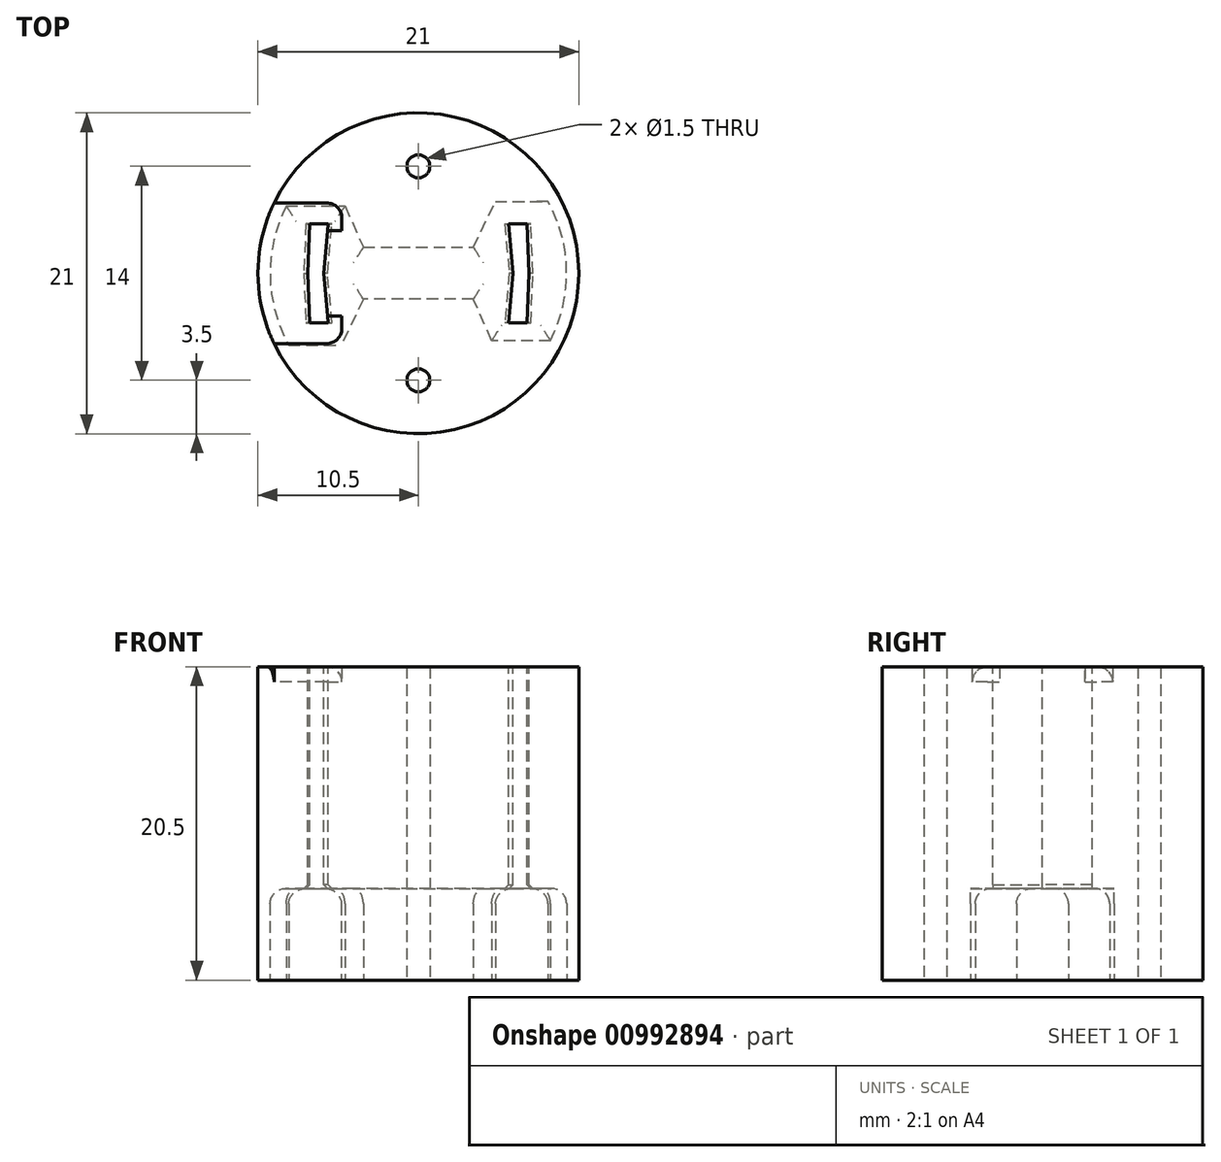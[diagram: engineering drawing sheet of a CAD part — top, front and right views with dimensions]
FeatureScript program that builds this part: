
annotation { "Feature Type Name" : "Feature", "Feature Type Description" : "" }
export const myFeature = defineFeature(function(context is Context, id is Id, definition is map)
    precondition{}
    {
        {
            var Q0;
            Q0=qCreatedBy(makeId("Top.planeOp"),FACE);
            var sketch = newSketch(context, id + "F0", { "sketchPlane" : qUnion([Q0])});
            skCircle(sketch, "E0", {"center": v(0, 0) * mm, "radius": 10.5 * mm});
            skSolve(sketch);
        }
        {
            var Q0;
            Q0=qSketchRegion(id+"F0",true);
            extrude(context, id + "F1", {"entities" : qUnion([Q0]), "oppositeDirection" : true, "depth" : 20.5 * mm});
        }
        {
            var Q0;
            Q0=makeQuery(id+"F1.opExtrude","CAP_FACE",FACE,{"disambiguationData":[OSD([sQuery(id+"F0.wireOp",EDGE,"E0")])],"isStart":false});
            var sketch = newSketch(context, id + "F2", { "sketchPlane" : qUnion([Q0])});
            skArc(sketch, "E1", {"start": v(-6.4, -5.2) * mm, "mid": v(-0.2, -8.25) * mm, "end": v(6.15, -5.5) * mm});
            skLineSegment(sketch, "E2", {"start": v(-8.49, 4.7) * mm, "end": v(-5.04, 4.7) * mm});
            skLineSegment(sketch, "E3", {"start": v(-8.64, -4.4) * mm, "end": v(-4.8, -4.4) * mm});
            skLineSegment(sketch, "E4", {"start": v(8.64, 4.4) * mm, "end": v(4.8, 4.4) * mm});
            skLineSegment(sketch, "E5", {"start": v(4.8, 4.4) * mm, "end": v(3.6, 1.7) * mm});
            skLineSegment(sketch, "E6", {"start": v(3.6, 1.7) * mm, "end": v(-3.6, 1.7) * mm});
            skLineSegment(sketch, "E7", {"start": v(-3.6, 1.7) * mm, "end": v(-5.04, 4.7) * mm});
            skLineSegment(sketch, "E8", {"start": v(-4, 4.4) * mm, "end": v(3.92, 4.4) * mm});
            skLineSegment(sketch, "E9", {"start": v(3.92, 4.4) * mm, "end": v(3.17, 2.7) * mm});
            skLineSegment(sketch, "E10", {"start": v(3.17, 2.7) * mm, "end": v(-3.2, 2.7) * mm});
            skLineSegment(sketch, "E11", {"start": v(-3.2, 2.7) * mm, "end": v(-4, 4.4) * mm});
            skLineSegment(sketch, "E12", {"start": v(-4.8, -4.4) * mm, "end": v(-3.6, -1.7) * mm});
            skLineSegment(sketch, "E13", {"start": v(-3.6, -1.7) * mm, "end": v(3.6, -1.7) * mm});
            skLineSegment(sketch, "E14", {"start": v(4, -4.4) * mm, "end": v(3.2, -2.7) * mm});
            skLineSegment(sketch, "E15", {"start": v(3.2, -2.7) * mm, "end": v(-3.17, -2.7) * mm});
            skLineSegment(sketch, "E16", {"start": v(-3.17, -2.7) * mm, "end": v(-3.92, -4.4) * mm});
            skLineSegment(sketch, "E17", {"start": v(-3.92, -4.4) * mm, "end": v(4, -4.4) * mm});
            skArc(sketch, "E18", {"start": v(-8.64, -4.4) * mm, "mid": v(-9.7, 0.17) * mm, "end": v(-8.49, 4.7) * mm});
            skArc(sketch, "E19", {"start": v(8.64, 4.4) * mm, "mid": v(9.7, -0.17) * mm, "end": v(8.49, -4.7) * mm});
            skLineSegment(sketch, "E20", {"start": v(6.15, -5.5) * mm, "end": v(2.15, -5.5) * mm});
            skLineSegment(sketch, "E21", {"start": v(3.6, -1.7) * mm, "end": v(5.04, -4.7) * mm});
            skLineSegment(sketch, "E22", {"start": v(5.04, -4.7) * mm, "end": v(8.49, -4.7) * mm});
            skLineSegment(sketch, "E23", {"start": v(-2.15, 5.5) * mm, "end": v(-6.15, 5.5) * mm});
            skLineSegment(sketch, "E24.trimOffspring", {"start": v(6.4, 5.2) * mm, "end": v(-2.15, 5.2) * mm});
            skArc(sketch, "E25.trimOffspring", {"start": v(-6.15, 5.5) * mm, "mid": v(0.2, 8.25) * mm, "end": v(6.4, 5.2) * mm});
            skLineSegment(sketch, "E26.trimOffspring", {"start": v(2.15, -5.2) * mm, "end": v(-6.4, -5.2) * mm});
            skLineSegment(sketch, "E27", {"start": v(2.15, -5.2) * mm, "end": v(2.15, -5.5) * mm});
            skLineSegment(sketch, "E28", {"start": v(-2.15, 5.5) * mm, "end": v(-2.15, 5.2) * mm});
            skSolve(sketch);
        }
        {
            var Q0;
            Q0=qSketchRegion(id+"F2",true);
            extrude(context, id + "F3", {"entities" : qUnion([Q0]), "operationType" : NewBodyOperationType.REMOVE, "oppositeDirection" : true, "depth" : 6 * mm});
        }
        {
            var Q0;
            Q0=makeQuery(id+"F1.opExtrude","CAP_FACE",FACE,{"disambiguationData":[OSD([sQuery(id+"F0.wireOp",EDGE,"E0")])],"isStart":false});
            var sketch = newSketch(context, id + "F4", { "sketchPlane" : qUnion([Q0])});
            skCircle(sketch, "E29", {"center": v(0, -7) * mm, "radius": 0.75 * mm});
            skCircle(sketch, "E30", {"center": v(0, 7) * mm, "radius": 0.75 * mm});
            skSolve(sketch);
        }
        {
            var Q0;
            Q0=qSketchRegion(id+"F4",true);
            extrude(context, id + "F5", {"entities" : qUnion([Q0]), "operationType" : NewBodyOperationType.REMOVE, "endBound" : BoundingType.THROUGH_ALL, "oppositeDirection" : true, "depth" : 30 * mm});
        }
        {
            var Q0;
            Q0=makeQuery(id+"F1.opExtrude","CAP_FACE",FACE,{"disambiguationData":[OSD([sQuery(id+"F0.wireOp",EDGE,"E0")])],"isStart":true});
            var sketch = newSketch(context, id + "F6", { "sketchPlane" : qUnion([Q0])});
            skLineSegment(sketch, "E31.bottom", {"start": v(-5, -2.8) * mm, "end": v(-6, -2.8) * mm});
            skLineSegment(sketch, "E31.right", {"start": v(-6, -2.8) * mm, "end": v(-6, 2.8) * mm});
            skArc(sketch, "E32", {"start": v(-9.44, 4.6) * mm, "mid": v(0, 10.5) * mm, "end": v(9.44, 4.6) * mm});
            skArc(sketch, "E33", {"start": v(9.44, -4.6) * mm, "mid": v(0, -10.5) * mm, "end": v(-9.44, -4.6) * mm});
            skLineSegment(sketch, "E34", {"start": v(-9.44, -4.6) * mm, "end": v(-5, -4.6) * mm});
            skLineSegment(sketch, "E35", {"start": v(-5, -4.6) * mm, "end": v(-5, -2.8) * mm});
            skLineSegment(sketch, "E36", {"start": v(-6, 2.8) * mm, "end": v(-5, 2.8) * mm});
            skLineSegment(sketch, "E37", {"start": v(-5, 2.8) * mm, "end": v(-5, 4.6) * mm});
            skLineSegment(sketch, "E38", {"start": v(-5, 4.6) * mm, "end": v(-9.44, 4.6) * mm});
            skLineSegment(sketch, "E39", {"start": v(9.44, 4.6) * mm, "end": v(5, 4.6) * mm});
            skLineSegment(sketch, "E40", {"start": v(5, 2.8) * mm, "end": v(6, 2.8) * mm});
            skLineSegment(sketch, "E41", {"start": v(6, 2.8) * mm, "end": v(6, -2.8) * mm});
            skLineSegment(sketch, "E42", {"start": v(6, -2.8) * mm, "end": v(5, -2.8) * mm});
            skLineSegment(sketch, "E43", {"start": v(5, -2.8) * mm, "end": v(5, -4.6) * mm});
            skLineSegment(sketch, "E44", {"start": v(5, -4.6) * mm, "end": v(9.44, -4.6) * mm});
            skLineSegment(sketch, "E45", {"start": v(5, 4.6) * mm, "end": v(5, 2.8) * mm});
            skSolve(sketch);
        }
        {
            var Q0;
            Q0=qSketchRegion(id+"F6",true);
            extrude(context, id + "F7", {"entities" : qUnion([Q0]), "operationType" : NewBodyOperationType.REMOVE, "oppositeDirection" : true, "depth" : 13 * mm});
        }
        {
            var Q0;
            {var subQ0=sQuery(id+"F0.wireOp",EDGE,"E0");Q0=makeQuery(id+"F7.boolean.opBoolean","SPLIT",FACE,{"disambiguationData":[TD([makeQuery(id+"F7.opExtrude","SWEPT_FACE",FACE,{"disambiguationData":[OSD([sQuery(id+"F6.wireOp",EDGE,"E31.bottom")])]})])],"derivedFrom":makeQuery(id+"F1.opExtrude","CAP_FACE",FACE,{"disambiguationData":[OSD([subQ0])],"isStart":true})});}
            var sketch = newSketch(context, id + "F8", { "sketchPlane" : qUnion([Q0])});
            skLineSegment(sketch, "E46", {"start": v(-5.9, -3.25) * mm, "end": v(-7.1, -3.25) * mm});
            skLineSegment(sketch, "E47", {"start": v(-7.1, -3.25) * mm, "end": v(-7.25, 0) * mm});
            skLineSegment(sketch, "E48", {"start": v(-7.25, 0) * mm, "end": v(-7.1, 3.25) * mm});
            skLineSegment(sketch, "E49", {"start": v(-7.1, 3.25) * mm, "end": v(-5.9, 3.25) * mm});
            skLineSegment(sketch, "E50", {"start": v(5.9, -3.25) * mm, "end": v(7.1, -3.25) * mm});
            skLineSegment(sketch, "E51", {"start": v(7.1, -3.25) * mm, "end": v(7.25, 0) * mm});
            skLineSegment(sketch, "E52", {"start": v(7.25, 0) * mm, "end": v(7.1, 3.25) * mm});
            skLineSegment(sketch, "E53", {"start": v(7.1, 3.25) * mm, "end": v(5.9, 3.25) * mm});
            skLineSegment(sketch, "E54", {"start": v(5.9, -3.25) * mm, "end": v(6.2, 0) * mm});
            skLineSegment(sketch, "E55", {"start": v(6.2, 0) * mm, "end": v(5.9, 3.25) * mm});
            skLineSegment(sketch, "E56", {"start": v(-5.9, 3.25) * mm, "end": v(-6.2, 0) * mm});
            skLineSegment(sketch, "E57", {"start": v(-5.9, -3.25) * mm, "end": v(-6.2, 0) * mm});
            skSolve(sketch);
        }
        {
            var Q0;
            Q0=qSketchRegion(id+"F8",true);
            extrude(context, id + "F9", {"entities" : qUnion([Q0]), "operationType" : NewBodyOperationType.REMOVE, "oppositeDirection" : true, "depth" : 25 * mm});
        }
        {
            var Q0;
            Q0=qCreatedBy(makeId("Right.planeOp"),FACE);
            cPlane(context, id + "F10", {"entities" : qUnion([Q0]), "cplaneType" : CPlaneType.OFFSET, "offset" : 7 * mm, "width" : 150 * mm, "height" : 150 * mm});
        }
        {
            var Q0;
            Q0=qCreatedBy(id+"F10.planeOp",FACE);
            var sketch = newSketch(context, id + "F11", { "sketchPlane" : qUnion([Q0])});
            skLineSegment(sketch, "E58", {"start": v(-2.8, 0) * mm, "end": v(-2.8, -13) * mm});
            skLineSegment(sketch, "E59", {"start": v(-2.8, -13) * mm, "end": v(0, -13) * mm});
            skLineSegment(sketch, "E60", {"start": v(0, -13) * mm, "end": v(2.8, -13) * mm});
            skLineSegment(sketch, "E61", {"start": v(2.8, -13) * mm, "end": v(2.8, 0) * mm});
            skLineSegment(sketch, "E62", {"start": v(2.8, 0) * mm, "end": v(-2.8, 0) * mm});
            skSolve(sketch);
        }
        {
            var Q0;
            Q0=qSketchRegion(id+"F11",true);
            extrude(context, id + "F12", {"entities" : qUnion([Q0]), "operationType" : NewBodyOperationType.REMOVE, "oppositeDirection" : true, "depth" : 14.04 * mm});
        }
        {
            var Q0;
            Q0=makeQuery(id+"F3.boolean.opBoolean","COPY",EDGE,{"derivedFrom":makeQuery(id+"F3.opExtrude","CAP_EDGE",EDGE,{"disambiguationData":[OSD([sQuery(id+"F2.wireOp",EDGE,"E6")])],"isStart":false})});
            var Q1;
            Q1=makeQuery(id+"F3.boolean.opBoolean","COPY",EDGE,{"derivedFrom":makeQuery(id+"F3.opExtrude","CAP_EDGE",EDGE,{"disambiguationData":[OSD([sQuery(id+"F2.wireOp",EDGE,"E13")])],"isStart":false})});
            var Q2;
            Q2=makeQuery(id+"F3.boolean.opBoolean","COPY",EDGE,{"derivedFrom":makeQuery(id+"F3.opExtrude","CAP_EDGE",EDGE,{"disambiguationData":[OSD([sQuery(id+"F2.wireOp",EDGE,"E21")])],"isStart":false})});
            var Q3;
            Q3=makeQuery(id+"F3.boolean.opBoolean","COPY",EDGE,{"derivedFrom":makeQuery(id+"F3.opExtrude","CAP_EDGE",EDGE,{"disambiguationData":[OSD([sQuery(id+"F2.wireOp",EDGE,"E7")])],"isStart":false})});
            var Q4;
            Q4=makeQuery(id+"F3.boolean.opBoolean","COPY",EDGE,{"derivedFrom":makeQuery(id+"F3.opExtrude","CAP_EDGE",EDGE,{"disambiguationData":[OSD([sQuery(id+"F2.wireOp",EDGE,"E19")])],"isStart":false})});
            var Q5;
            Q5=makeQuery(id+"F3.boolean.opBoolean","COPY",EDGE,{"derivedFrom":makeQuery(id+"F3.opExtrude","CAP_EDGE",EDGE,{"disambiguationData":[OSD([sQuery(id+"F2.wireOp",EDGE,"E4")])],"isStart":false})});
            var Q6;
            Q6=makeQuery(id+"F3.boolean.opBoolean","COPY",EDGE,{"derivedFrom":makeQuery(id+"F3.opExtrude","CAP_EDGE",EDGE,{"disambiguationData":[OSD([sQuery(id+"F2.wireOp",EDGE,"E18")])],"isStart":false})});
            var Q7;
            Q7=makeQuery(id+"F3.boolean.opBoolean","COPY",EDGE,{"derivedFrom":makeQuery(id+"F3.opExtrude","CAP_EDGE",EDGE,{"disambiguationData":[OSD([sQuery(id+"F2.wireOp",EDGE,"E3")])],"isStart":false})});
            var Q8;
            Q8=makeQuery(id+"F3.boolean.opBoolean","COPY",EDGE,{"derivedFrom":makeQuery(id+"F3.opExtrude","CAP_EDGE",EDGE,{"disambiguationData":[OSD([sQuery(id+"F2.wireOp",EDGE,"E12")])],"isStart":false})});
            var Q9;
            Q9=makeQuery(id+"F3.boolean.opBoolean","COPY",EDGE,{"derivedFrom":makeQuery(id+"F3.opExtrude","CAP_EDGE",EDGE,{"disambiguationData":[OSD([sQuery(id+"F2.wireOp",EDGE,"E5")])],"isStart":false})});
            fillet(context, id + "F13", {"entities" : qUnion([Q0, Q1, Q2, Q3, Q4, Q5, Q6, Q7, Q8, Q9]), "radius" : 1 * mm, "tangentPropagation" : true, "allowEdgeOverflow" : false});
        }
        {
            var Q0;
            Q0=makeQuery(id+"F9.boolean.opBoolean","INTERSECT",EDGE,{"derivedFrom":[makeQuery(id+"F3.boolean.opBoolean","COPY",FACE,{"derivedFrom":makeQuery(id+"F3.opExtrude","CAP_FACE",FACE,{"disambiguationData":[OSD([sQuery(id+"F2.wireOp",EDGE,"E2"),sQuery(id+"F2.wireOp",EDGE,"E3"),sQuery(id+"F2.wireOp",EDGE,"E4"),sQuery(id+"F2.wireOp",EDGE,"E5"),sQuery(id+"F2.wireOp",EDGE,"E6"),sQuery(id+"F2.wireOp",EDGE,"E7"),sQuery(id+"F2.wireOp",EDGE,"E12"),sQuery(id+"F2.wireOp",EDGE,"E13"),sQuery(id+"F2.wireOp",EDGE,"E18"),sQuery(id+"F2.wireOp",EDGE,"E19"),sQuery(id+"F2.wireOp",EDGE,"E21"),sQuery(id+"F2.wireOp",EDGE,"E22")])],"isStart":false})}),makeQuery(id+"F9.opExtrude","SWEPT_FACE",FACE,{"disambiguationData":[OSD([sQuery(id+"F8.wireOp",EDGE,"E51")])]})]});
            var Q1;
            Q1=makeQuery(id+"F9.boolean.opBoolean","INTERSECT",EDGE,{"derivedFrom":[makeQuery(id+"F3.boolean.opBoolean","COPY",FACE,{"derivedFrom":makeQuery(id+"F3.opExtrude","CAP_FACE",FACE,{"disambiguationData":[OSD([sQuery(id+"F2.wireOp",EDGE,"E2"),sQuery(id+"F2.wireOp",EDGE,"E3"),sQuery(id+"F2.wireOp",EDGE,"E4"),sQuery(id+"F2.wireOp",EDGE,"E5"),sQuery(id+"F2.wireOp",EDGE,"E6"),sQuery(id+"F2.wireOp",EDGE,"E7"),sQuery(id+"F2.wireOp",EDGE,"E12"),sQuery(id+"F2.wireOp",EDGE,"E13"),sQuery(id+"F2.wireOp",EDGE,"E18"),sQuery(id+"F2.wireOp",EDGE,"E19"),sQuery(id+"F2.wireOp",EDGE,"E21"),sQuery(id+"F2.wireOp",EDGE,"E22")])],"isStart":false})}),makeQuery(id+"F9.opExtrude","SWEPT_FACE",FACE,{"disambiguationData":[OSD([sQuery(id+"F8.wireOp",EDGE,"E52")])]})]});
            var Q2;
            Q2=makeQuery(id+"F9.boolean.opBoolean","INTERSECT",EDGE,{"derivedFrom":[makeQuery(id+"F3.boolean.opBoolean","COPY",FACE,{"derivedFrom":makeQuery(id+"F3.opExtrude","CAP_FACE",FACE,{"disambiguationData":[OSD([sQuery(id+"F2.wireOp",EDGE,"E2"),sQuery(id+"F2.wireOp",EDGE,"E3"),sQuery(id+"F2.wireOp",EDGE,"E4"),sQuery(id+"F2.wireOp",EDGE,"E5"),sQuery(id+"F2.wireOp",EDGE,"E6"),sQuery(id+"F2.wireOp",EDGE,"E7"),sQuery(id+"F2.wireOp",EDGE,"E12"),sQuery(id+"F2.wireOp",EDGE,"E13"),sQuery(id+"F2.wireOp",EDGE,"E18"),sQuery(id+"F2.wireOp",EDGE,"E19"),sQuery(id+"F2.wireOp",EDGE,"E21"),sQuery(id+"F2.wireOp",EDGE,"E22")])],"isStart":false})}),makeQuery(id+"F9.opExtrude","SWEPT_FACE",FACE,{"disambiguationData":[OSD([sQuery(id+"F8.wireOp",EDGE,"E47")])]})]});
            var Q3;
            Q3=makeQuery(id+"F9.boolean.opBoolean","INTERSECT",EDGE,{"derivedFrom":[makeQuery(id+"F3.boolean.opBoolean","COPY",FACE,{"derivedFrom":makeQuery(id+"F3.opExtrude","CAP_FACE",FACE,{"disambiguationData":[OSD([sQuery(id+"F2.wireOp",EDGE,"E2"),sQuery(id+"F2.wireOp",EDGE,"E3"),sQuery(id+"F2.wireOp",EDGE,"E4"),sQuery(id+"F2.wireOp",EDGE,"E5"),sQuery(id+"F2.wireOp",EDGE,"E6"),sQuery(id+"F2.wireOp",EDGE,"E7"),sQuery(id+"F2.wireOp",EDGE,"E12"),sQuery(id+"F2.wireOp",EDGE,"E13"),sQuery(id+"F2.wireOp",EDGE,"E18"),sQuery(id+"F2.wireOp",EDGE,"E19"),sQuery(id+"F2.wireOp",EDGE,"E21"),sQuery(id+"F2.wireOp",EDGE,"E22")])],"isStart":false})}),makeQuery(id+"F9.opExtrude","SWEPT_FACE",FACE,{"disambiguationData":[OSD([sQuery(id+"F8.wireOp",EDGE,"E48")])]})]});
            var Q4;
            Q4=makeQuery(id+"F9.boolean.opBoolean","INTERSECT",EDGE,{"derivedFrom":[makeQuery(id+"F3.boolean.opBoolean","COPY",FACE,{"derivedFrom":makeQuery(id+"F3.opExtrude","CAP_FACE",FACE,{"disambiguationData":[OSD([sQuery(id+"F2.wireOp",EDGE,"E2"),sQuery(id+"F2.wireOp",EDGE,"E3"),sQuery(id+"F2.wireOp",EDGE,"E4"),sQuery(id+"F2.wireOp",EDGE,"E5"),sQuery(id+"F2.wireOp",EDGE,"E6"),sQuery(id+"F2.wireOp",EDGE,"E7"),sQuery(id+"F2.wireOp",EDGE,"E12"),sQuery(id+"F2.wireOp",EDGE,"E13"),sQuery(id+"F2.wireOp",EDGE,"E18"),sQuery(id+"F2.wireOp",EDGE,"E19"),sQuery(id+"F2.wireOp",EDGE,"E21"),sQuery(id+"F2.wireOp",EDGE,"E22")])],"isStart":false})}),makeQuery(id+"F9.opExtrude","SWEPT_FACE",FACE,{"disambiguationData":[OSD([sQuery(id+"F8.wireOp",EDGE,"E54")])]})]});
            var Q5;
            Q5=makeQuery(id+"F9.boolean.opBoolean","INTERSECT",EDGE,{"derivedFrom":[makeQuery(id+"F3.boolean.opBoolean","COPY",FACE,{"derivedFrom":makeQuery(id+"F3.opExtrude","CAP_FACE",FACE,{"disambiguationData":[OSD([sQuery(id+"F2.wireOp",EDGE,"E2"),sQuery(id+"F2.wireOp",EDGE,"E3"),sQuery(id+"F2.wireOp",EDGE,"E4"),sQuery(id+"F2.wireOp",EDGE,"E5"),sQuery(id+"F2.wireOp",EDGE,"E6"),sQuery(id+"F2.wireOp",EDGE,"E7"),sQuery(id+"F2.wireOp",EDGE,"E12"),sQuery(id+"F2.wireOp",EDGE,"E13"),sQuery(id+"F2.wireOp",EDGE,"E18"),sQuery(id+"F2.wireOp",EDGE,"E19"),sQuery(id+"F2.wireOp",EDGE,"E21"),sQuery(id+"F2.wireOp",EDGE,"E22")])],"isStart":false})}),makeQuery(id+"F9.opExtrude","SWEPT_FACE",FACE,{"disambiguationData":[OSD([sQuery(id+"F8.wireOp",EDGE,"E55")])]})]});
            var Q6;
            Q6=makeQuery(id+"F9.boolean.opBoolean","INTERSECT",EDGE,{"derivedFrom":[makeQuery(id+"F3.boolean.opBoolean","COPY",FACE,{"derivedFrom":makeQuery(id+"F3.opExtrude","CAP_FACE",FACE,{"disambiguationData":[OSD([sQuery(id+"F2.wireOp",EDGE,"E2"),sQuery(id+"F2.wireOp",EDGE,"E3"),sQuery(id+"F2.wireOp",EDGE,"E4"),sQuery(id+"F2.wireOp",EDGE,"E5"),sQuery(id+"F2.wireOp",EDGE,"E6"),sQuery(id+"F2.wireOp",EDGE,"E7"),sQuery(id+"F2.wireOp",EDGE,"E12"),sQuery(id+"F2.wireOp",EDGE,"E13"),sQuery(id+"F2.wireOp",EDGE,"E18"),sQuery(id+"F2.wireOp",EDGE,"E19"),sQuery(id+"F2.wireOp",EDGE,"E21"),sQuery(id+"F2.wireOp",EDGE,"E22")])],"isStart":false})}),makeQuery(id+"F9.opExtrude","SWEPT_FACE",FACE,{"disambiguationData":[OSD([sQuery(id+"F8.wireOp",EDGE,"E57")])]})]});
            var Q7;
            Q7=makeQuery(id+"F9.boolean.opBoolean","INTERSECT",EDGE,{"derivedFrom":[makeQuery(id+"F3.boolean.opBoolean","COPY",FACE,{"derivedFrom":makeQuery(id+"F3.opExtrude","CAP_FACE",FACE,{"disambiguationData":[OSD([sQuery(id+"F2.wireOp",EDGE,"E2"),sQuery(id+"F2.wireOp",EDGE,"E3"),sQuery(id+"F2.wireOp",EDGE,"E4"),sQuery(id+"F2.wireOp",EDGE,"E5"),sQuery(id+"F2.wireOp",EDGE,"E6"),sQuery(id+"F2.wireOp",EDGE,"E7"),sQuery(id+"F2.wireOp",EDGE,"E12"),sQuery(id+"F2.wireOp",EDGE,"E13"),sQuery(id+"F2.wireOp",EDGE,"E18"),sQuery(id+"F2.wireOp",EDGE,"E19"),sQuery(id+"F2.wireOp",EDGE,"E21"),sQuery(id+"F2.wireOp",EDGE,"E22")])],"isStart":false})}),makeQuery(id+"F9.opExtrude","SWEPT_FACE",FACE,{"disambiguationData":[OSD([sQuery(id+"F8.wireOp",EDGE,"E56")])]})]});
            chamfer(context, id + "F14", {"entities" : qUnion([Q0, Q1, Q2, Q3, Q4, Q5, Q6, Q7]), "width" : .25 * mm, "tangentPropagation" : true});
        }
        {
            var Q0;
            Q0=makeQuery(id+"F2.imprint","IMPRINT",FACE,{"disambiguationData":[TD([[makeQuery(id+"F2.imprint","IMPRINT",EDGE,{"derivedFrom":sQuery(id+"F2.wireOp",EDGE,"E23")}),-1.0]])]});
            var sketch = newSketch(context, id + "F15", { "sketchPlane" : qUnion([Q0])});
            skLineSegment(sketch, "E63.0", {"start": v(0.7, 6.76) * mm, "end": v(0.7, 6.76) * mm});
            skLineSegment(sketch, "E64.0.0", {"start": v(-6.15, 5.5) * mm, "end": v(-2.15, 5.5) * mm});
            skLineSegment(sketch, "E64.0.1", {"start": v(-2.15, 5.5) * mm, "end": v(-2.15, 5.2) * mm});
            skLineSegment(sketch, "E64.0.2", {"start": v(-2.15, 5.2) * mm, "end": v(6.4, 5.2) * mm});
            skArc(sketch, "E64.0.3", {"start": v(6.4, 5.2) * mm, "mid": v(0.2, 8.25) * mm, "end": v(-6.15, 5.5) * mm});
            skLineSegment(sketch, "E65.0", {"start": v(-0.7, -6.72) * mm, "end": v(-0.7, -6.72) * mm});
            skLineSegment(sketch, "E66.0.0", {"start": v(2.15, -5.2) * mm, "end": v(-6.4, -5.2) * mm});
            skArc(sketch, "E66.0.1", {"start": v(-6.4, -5.2) * mm, "mid": v(-0.2, -8.25) * mm, "end": v(6.15, -5.5) * mm});
            skLineSegment(sketch, "E66.0.2", {"start": v(6.15, -5.5) * mm, "end": v(2.15, -5.5) * mm});
            skLineSegment(sketch, "E66.0.3", {"start": v(2.15, -5.5) * mm, "end": v(2.15, -5.2) * mm});
            skCircle(sketch, "E67.0", {"center": v(0, 7) * mm, "radius": 0.75 * mm});
            skCircle(sketch, "E68.0", {"center": v(0, -7) * mm, "radius": 0.75 * mm});
            skSolve(sketch);
        }
        {
            var Q0;
            Q0=makeQuery(id+"F2.imprint","IMPRINT",FACE,{"disambiguationData":[TD([[makeQuery(id+"F2.imprint","IMPRINT",EDGE,{"derivedFrom":sQuery(id+"F2.wireOp",EDGE,"E1")}),-1.0]])]});
            var sketch = newSketch(context, id + "F16", { "sketchPlane" : qUnion([Q0])});
            skLineSegment(sketch, "E69.0.0", {"start": v(2.15, -5.2) * mm, "end": v(-6.4, -5.2) * mm});
            skArc(sketch, "E69.0.1", {"start": v(-6.4, -5.2) * mm, "mid": v(-0.2, -8.25) * mm, "end": v(6.15, -5.5) * mm});
            skLineSegment(sketch, "E69.0.2", {"start": v(6.15, -5.5) * mm, "end": v(2.15, -5.5) * mm});
            skLineSegment(sketch, "E69.0.3", {"start": v(2.15, -5.5) * mm, "end": v(2.15, -5.2) * mm});
            skLineSegment(sketch, "E70.0.0", {"start": v(-3.92, -4.4) * mm, "end": v(4, -4.4) * mm});
            skLineSegment(sketch, "E70.0.1", {"start": v(4, -4.4) * mm, "end": v(3.2, -2.7) * mm});
            skLineSegment(sketch, "E70.0.2", {"start": v(3.2, -2.7) * mm, "end": v(-3.17, -2.7) * mm});
            skLineSegment(sketch, "E70.0.3", {"start": v(-3.17, -2.7) * mm, "end": v(-3.92, -4.4) * mm});
            skLineSegment(sketch, "E71.0.0", {"start": v(3.92, 4.4) * mm, "end": v(-4, 4.4) * mm});
            skLineSegment(sketch, "E71.0.1", {"start": v(-4, 4.4) * mm, "end": v(-3.2, 2.7) * mm});
            skLineSegment(sketch, "E71.0.2", {"start": v(-3.2, 2.7) * mm, "end": v(3.17, 2.7) * mm});
            skLineSegment(sketch, "E71.0.3", {"start": v(3.17, 2.7) * mm, "end": v(3.92, 4.4) * mm});
            skLineSegment(sketch, "E72.0.0", {"start": v(-6.15, 5.5) * mm, "end": v(-2.15, 5.5) * mm});
            skLineSegment(sketch, "E72.0.1", {"start": v(-2.15, 5.5) * mm, "end": v(-2.15, 5.2) * mm});
            skLineSegment(sketch, "E72.0.2", {"start": v(-2.15, 5.2) * mm, "end": v(6.4, 5.2) * mm});
            skArc(sketch, "E72.0.3", {"start": v(6.4, 5.2) * mm, "mid": v(0.2, 8.25) * mm, "end": v(-6.15, 5.5) * mm});
            skSolve(sketch);
        }
        {
            var Q0;
            Q0=qSketchRegion(id+"F16",true);
            extrude(context, id + "F17", {"entities" : qUnion([Q0]), "operationType" : NewBodyOperationType.ADD, "oppositeDirection" : true, "depth" : 6 * mm});
        }
        {
            var Q0;
            Q0=makeQuery(id+"F2.imprint","IMPRINT",FACE,{"disambiguationData":[TD([[makeQuery(id+"F2.imprint","IMPRINT",EDGE,{"derivedFrom":sQuery(id+"F2.wireOp",EDGE,"E1")}),-1.0]])]});
            var sketch = newSketch(context, id + "F18", { "sketchPlane" : qUnion([Q0])});
            skCircle(sketch, "E73.0", {"center": v(0, 7) * mm, "radius": 0.75 * mm});
            skCircle(sketch, "E74.0", {"center": v(0, -7) * mm, "radius": 0.75 * mm});
            skSolve(sketch);
        }
        {
            var Q0;
            Q0=qSketchRegion(id+"F18",true);
            extrude(context, id + "F19", {"entities" : qUnion([Q0]), "operationType" : NewBodyOperationType.REMOVE, "oppositeDirection" : true, "depth" : 25 * mm});
        }
        {
            var Q0;
            Q0=makeQuery(id+"F7.boolean.opBoolean","COPY",EDGE,{"derivedFrom":makeQuery(id+"F7.opExtrude","CAP_EDGE",EDGE,{"disambiguationData":[OSD([sQuery(id+"F6.wireOp",EDGE,"E34")])],"isStart":true})});
            var Q1;
            Q1=makeQuery(id+"F7.boolean.opBoolean","COPY",EDGE,{"derivedFrom":makeQuery(id+"F7.opExtrude","CAP_EDGE",EDGE,{"disambiguationData":[OSD([sQuery(id+"F6.wireOp",EDGE,"E35")])],"isStart":true})});
            var Q2;
            Q2=makeQuery(id+"F7.boolean.opBoolean","COPY",EDGE,{"derivedFrom":makeQuery(id+"F7.opExtrude","CAP_EDGE",EDGE,{"disambiguationData":[OSD([sQuery(id+"F6.wireOp",EDGE,"E37")])],"isStart":true})});
            var Q3;
            Q3=makeQuery(id+"F7.boolean.opBoolean","COPY",EDGE,{"derivedFrom":makeQuery(id+"F7.opExtrude","CAP_EDGE",EDGE,{"disambiguationData":[OSD([sQuery(id+"F6.wireOp",EDGE,"E38")])],"isStart":true})});
            var Q4;
            Q4=makeQuery(id+"F7.boolean.opBoolean","COPY",EDGE,{"derivedFrom":makeQuery(id+"F7.opExtrude","CAP_EDGE",EDGE,{"disambiguationData":[OSD([sQuery(id+"F6.wireOp",EDGE,"E44")])],"isStart":true})});
            var Q5;
            Q5=makeQuery(id+"F7.boolean.opBoolean","COPY",EDGE,{"derivedFrom":makeQuery(id+"F7.opExtrude","CAP_EDGE",EDGE,{"disambiguationData":[OSD([sQuery(id+"F6.wireOp",EDGE,"E43")])],"isStart":true})});
            var Q6;
            Q6=makeQuery(id+"F7.boolean.opBoolean","COPY",EDGE,{"derivedFrom":makeQuery(id+"F7.opExtrude","CAP_EDGE",EDGE,{"disambiguationData":[OSD([sQuery(id+"F6.wireOp",EDGE,"E45")])],"isStart":true})});
            var Q7;
            Q7=makeQuery(id+"F7.boolean.opBoolean","COPY",EDGE,{"derivedFrom":makeQuery(id+"F7.opExtrude","CAP_EDGE",EDGE,{"disambiguationData":[OSD([sQuery(id+"F6.wireOp",EDGE,"E39")])],"isStart":true})});
            fillet(context, id + "F20", {"entities" : qUnion([Q0, Q1, Q2, Q3, Q4, Q5, Q6, Q7]), "radius" : 1 * mm, "tangentPropagation" : true, "allowEdgeOverflow" : false});
        }
        {
            var Q0;
            Q0=makeQuery(id+"F20.opFillet","BLEND_EDGE",EDGE,{"blendedFrom":[makeQuery(id+"F7.boolean.opBoolean","COPY",EDGE,{"derivedFrom":makeQuery(id+"F7.opExtrude","CAP_EDGE",EDGE,{"disambiguationData":[OSD([sQuery(id+"F6.wireOp",EDGE,"E34")])],"isStart":true})}),makeQuery(id+"F7.boolean.opBoolean","COPY",EDGE,{"derivedFrom":makeQuery(id+"F7.opExtrude","CAP_EDGE",EDGE,{"disambiguationData":[OSD([sQuery(id+"F6.wireOp",EDGE,"E35")])],"isStart":true})})],"blendedInto":[]});
            var Q1;
            Q1=makeQuery(id+"F20.opFillet","BLEND_EDGE",EDGE,{"blendedFrom":[makeQuery(id+"F7.boolean.opBoolean","COPY",EDGE,{"derivedFrom":makeQuery(id+"F7.opExtrude","CAP_EDGE",EDGE,{"disambiguationData":[OSD([sQuery(id+"F6.wireOp",EDGE,"E43")])],"isStart":true})}),makeQuery(id+"F7.boolean.opBoolean","COPY",EDGE,{"derivedFrom":makeQuery(id+"F7.opExtrude","CAP_EDGE",EDGE,{"disambiguationData":[OSD([sQuery(id+"F6.wireOp",EDGE,"E44")])],"isStart":true})})],"blendedInto":[]});
            var Q2;
            Q2=makeQuery(id+"F20.opFillet","BLEND_EDGE",EDGE,{"blendedFrom":[makeQuery(id+"F7.boolean.opBoolean","COPY",EDGE,{"derivedFrom":makeQuery(id+"F7.opExtrude","CAP_EDGE",EDGE,{"disambiguationData":[OSD([sQuery(id+"F6.wireOp",EDGE,"E37")])],"isStart":true})}),makeQuery(id+"F7.boolean.opBoolean","COPY",EDGE,{"derivedFrom":makeQuery(id+"F7.opExtrude","CAP_EDGE",EDGE,{"disambiguationData":[OSD([sQuery(id+"F6.wireOp",EDGE,"E38")])],"isStart":true})})],"blendedInto":[]});
            var Q3;
            Q3=makeQuery(id+"F20.opFillet","BLEND_EDGE",EDGE,{"blendedFrom":[makeQuery(id+"F7.boolean.opBoolean","COPY",EDGE,{"derivedFrom":makeQuery(id+"F7.opExtrude","CAP_EDGE",EDGE,{"disambiguationData":[OSD([sQuery(id+"F6.wireOp",EDGE,"E39")])],"isStart":true})}),makeQuery(id+"F7.boolean.opBoolean","COPY",EDGE,{"derivedFrom":makeQuery(id+"F7.opExtrude","CAP_EDGE",EDGE,{"disambiguationData":[OSD([sQuery(id+"F6.wireOp",EDGE,"E45")])],"isStart":true})})],"blendedInto":[]});
            fillet(context, id + "F21", {"entities" : qUnion([Q0, Q1, Q2, Q3]), "radius" : 1 * mm, "tangentPropagation" : true, "allowEdgeOverflow" : false});
        }
        {
            var Q0;
            Q0=makeQuery(id+"F12.boolean.opBoolean","MERGE",FACE,{"derivedFrom":[makeQuery(id+"F7.boolean.opBoolean","COPY",FACE,{"derivedFrom":makeQuery(id+"F7.opExtrude","CAP_FACE",FACE,{"disambiguationData":[OSD([sQuery(id+"F6.wireOp",EDGE,"E31.bottom"),sQuery(id+"F6.wireOp",EDGE,"E31.right"),sQuery(id+"F6.wireOp",EDGE,"E32"),sQuery(id+"F6.wireOp",EDGE,"E33"),sQuery(id+"F6.wireOp",EDGE,"E34"),sQuery(id+"F6.wireOp",EDGE,"E35"),sQuery(id+"F6.wireOp",EDGE,"E36"),sQuery(id+"F6.wireOp",EDGE,"E37"),sQuery(id+"F6.wireOp",EDGE,"E38"),sQuery(id+"F6.wireOp",EDGE,"E39"),sQuery(id+"F6.wireOp",EDGE,"E40"),sQuery(id+"F6.wireOp",EDGE,"E41"),sQuery(id+"F6.wireOp",EDGE,"E42"),sQuery(id+"F6.wireOp",EDGE,"E43"),sQuery(id+"F6.wireOp",EDGE,"E44"),sQuery(id+"F6.wireOp",EDGE,"E45")])],"isStart":false})}),makeQuery(id+"F12.opExtrude","SWEPT_FACE",FACE,{"disambiguationData":[OSD([sQuery(id+"F11.wireOp",EDGE,"E59"),sQuery(id+"F11.wireOp",EDGE,"E60")])]})]});
            extrude(context, id + "F22", {"entities" : qUnion([Q0]), "operationType" : NewBodyOperationType.ADD, "depth" : 13 * mm});
        }
    });
